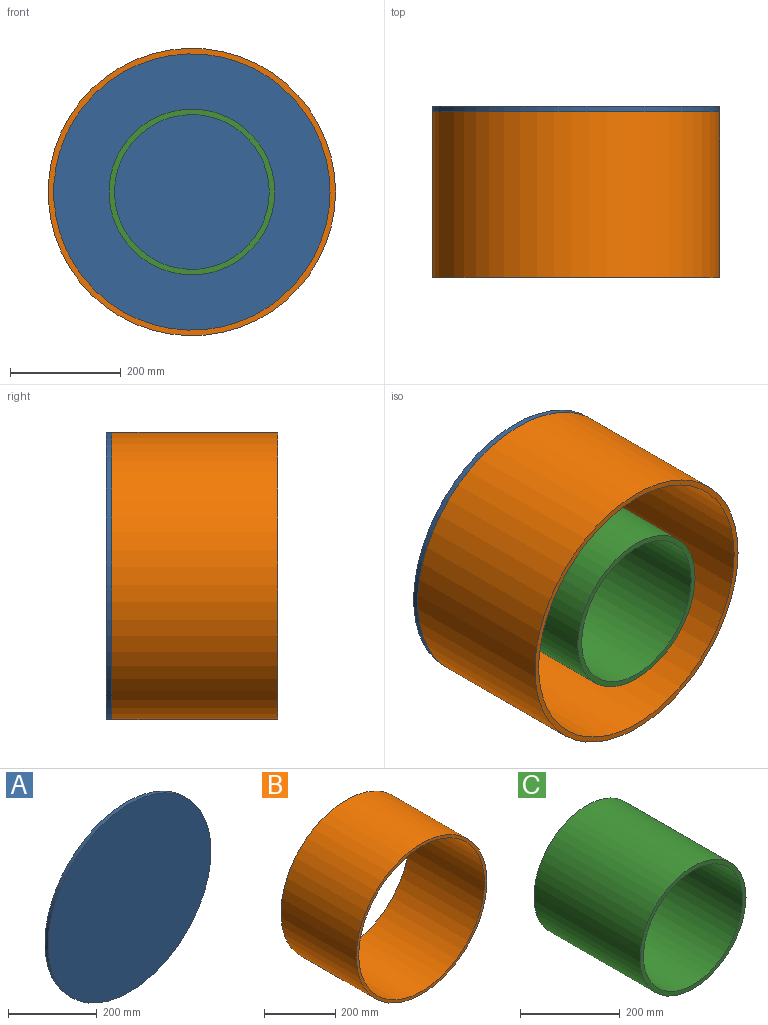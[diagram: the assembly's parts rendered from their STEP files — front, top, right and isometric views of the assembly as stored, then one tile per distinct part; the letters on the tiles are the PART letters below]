
ASSEMBLY  parts=3 mates=2
PART A: 3 faces, bbox 520x10x520 mm
  f0: cylinder r=260mm len=520mm, axis (0,1,0), area 16336.3mm2, adj f1,f2
  f1: plane 520x520mm, normal (0,-1,0), area 212371.7mm2, adj f0
  f2: plane 520x520mm, normal (0,1,0), area 212371.7mm2, adj f0
PART B: 4 faces, bbox 520x300x520 mm
  f0: cylinder r=250mm len=500mm, axis (0,1,0), area 471238.9mm2, adj f2,f3
  f1: cylinder r=260mm len=520mm, axis (0,1,0), area 490088.5mm2, adj f2,f3
  f2: plane 520x520mm, normal (0,-1,0), area 16022.1mm2, adj f0,f1
  f3: plane 520x520mm, normal (0,1,0), area 16022.1mm2, adj f0,f1
PART C: 4 faces, bbox 300x300x300 mm
  f0: cylinder r=140mm len=300mm, axis (0,1,0), area 263893.8mm2, adj f2,f3
  f1: cylinder r=150mm len=300mm, axis (0,1,0), area 282743.3mm2, adj f2,f3
  f2: plane 300x300mm, normal (0,-1,0), area 9110.6mm2, adj f0,f1
  f3: plane 300x300mm, normal (0,1,0), area 9110.6mm2, adj f0,f1
PLACE A t=(-38.61,139.76,3.08)mm
PLACE B t=(-38.61,129.76,3.08)mm
PLACE C t=(-38.61,129.76,3.08)mm
MATE fastened C.f0 <-> A.f0  axis (0,1,0) through (-38.61,129.76,3.08)mm
MATE fastened A.f0 <-> B.f0  axis (0,-1,0) through (-38.61,129.76,3.08)mm
